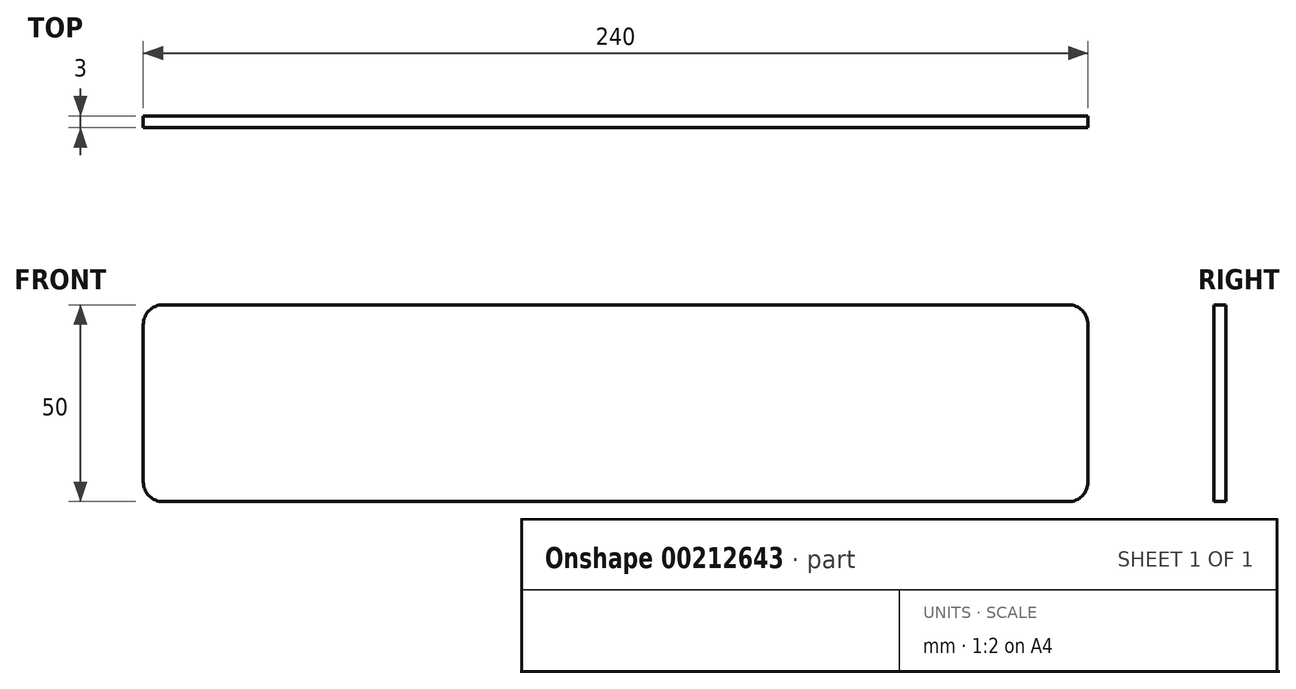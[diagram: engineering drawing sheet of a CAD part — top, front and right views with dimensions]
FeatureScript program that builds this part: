
annotation { "Feature Type Name" : "Feature", "Feature Type Description" : "" }
export const myFeature = defineFeature(function(context is Context, id is Id, definition is map)
    precondition{}
    {
        {
            var Q0;
            Q0=qCreatedBy(makeId("Front.planeOp"),FACE);
            var sketch = newSketch(context, id + "F0", { "sketchPlane" : qUnion([Q0])});
            skLineSegment(sketch, "E0.bottom", {"start": v(-120, 25) * mm, "end": v(120, 25) * mm});
            skLineSegment(sketch, "E0.top", {"start": v(-120, -25) * mm, "end": v(120, -25) * mm});
            skLineSegment(sketch, "E0.left", {"start": v(-120, 25) * mm, "end": v(-120, -25) * mm});
            skLineSegment(sketch, "E0.right", {"start": v(120, 25) * mm, "end": v(120, -25) * mm});
            skSolve(sketch);
        }
        {
            var Q0;
            Q0 = qSketchRegion(id + "F0", true);
            extrude(context, id + "F1", {"entities" : qUnion([Q0]), "depth" : 3 * mm});
        }
        {
            var Q0;
            Q0=makeQuery(id+"F1.opExtrude","SWEPT_EDGE",EDGE,{"disambiguationData":[OSD([sQuery(id+"F0.wireOp",EDGE,"E0.bottom"),sQuery(id+"F0.wireOp",EDGE,"E0.left")])]});
            var Q1;
            Q1=makeQuery(id+"F1.opExtrude","SWEPT_EDGE",EDGE,{"disambiguationData":[OSD([sQuery(id+"F0.wireOp",EDGE,"E0.top"),sQuery(id+"F0.wireOp",EDGE,"E0.left")])]});
            var Q2;
            Q2=makeQuery(id+"F1.opExtrude","SWEPT_EDGE",EDGE,{"disambiguationData":[OSD([sQuery(id+"F0.wireOp",EDGE,"E0.bottom"),sQuery(id+"F0.wireOp",EDGE,"E0.right")])]});
            var Q3;
            Q3=makeQuery(id+"F1.opExtrude","SWEPT_EDGE",EDGE,{"disambiguationData":[OSD([sQuery(id+"F0.wireOp",EDGE,"E0.top"),sQuery(id+"F0.wireOp",EDGE,"E0.right")])]});
            fillet(context, id + "F2", {"entities" : qUnion([Q0, Q1, Q2, Q3]), "radius" : 5 * mm, "tangentPropagation" : true, "allowEdgeOverflow" : false});
        }
    });
